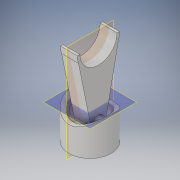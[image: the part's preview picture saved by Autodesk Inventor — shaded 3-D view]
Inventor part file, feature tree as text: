
AUTODESK INVENTOR PART (.ipt)
format: ipt  version: 2018 (Build 220112000, 112)  size: 168,960 bytes
history: native  units: in
note: dims shown in document units (in); Inventor stores cm internally (conversion verified against a paired STEP export)
features: sketch x7, extrude x7, projected_geometry x2, plane x1
ambient origin geometry x8: Origin, YZ Plane, XZ Plane, XY Plane, X Axis, Y Axis, Z Axis, Center Point
bodies: Solid1 (feature_tree)
feature tree (17):
  sketch  "Sketch1"  dims[d0=0.5in d1=0.3in d2=0.0in]
  extrude  "Extrusion1"  Depth=0.3in TaperAngle=0.0deg
  extrude  "Extrusion2"  Depth=0.1in
  plane  "Work Plane1"
  extrude  "Extrusion3"  [1 undecoded]
  extrude  "Extrusion4"  Depth=0.25in TaperAngle=0.0deg
  extrude  "Extrusion5"  Depth=0.1in
  extrude  "Extrusion6"  Depth=0.14in
  extrude  "Extrusion7"  Depth=0.1in
  sketch  "Sketch2"  dims[d5=0.1in d6=0.35in]
  sketch  "Sketch3"  dims[d7=1.0in d8=0.0in d9=-0.3in]
  sketch  "Sketch4"  dims[d10=0.4in d11=0.25in d12=0.0in]
  sketch  "Sketch5"  dims[d13=0.1in d14=0.1in]
  sketch  "Sketch6"  dims[d15=0.45in d16=0.0in d17=0.14in]
  projected_geometry  "Projected Loop1"
  sketch  "Sketch7"  dims[d18=0.18in d21=0.44in d22=0.0in d23=0.8in d26=0.5in d27=0.2in d28=0.0in d29=1.0in d30=0.0in d31=0.1in d32=0.0in]
  projected_geometry  "Projected Loop2"
note: 1 required parameter value undecoded (feature->parameter linkage not recoverable at this tier; creation-order binding heuristic only, values carry confidence <= 0.55)
